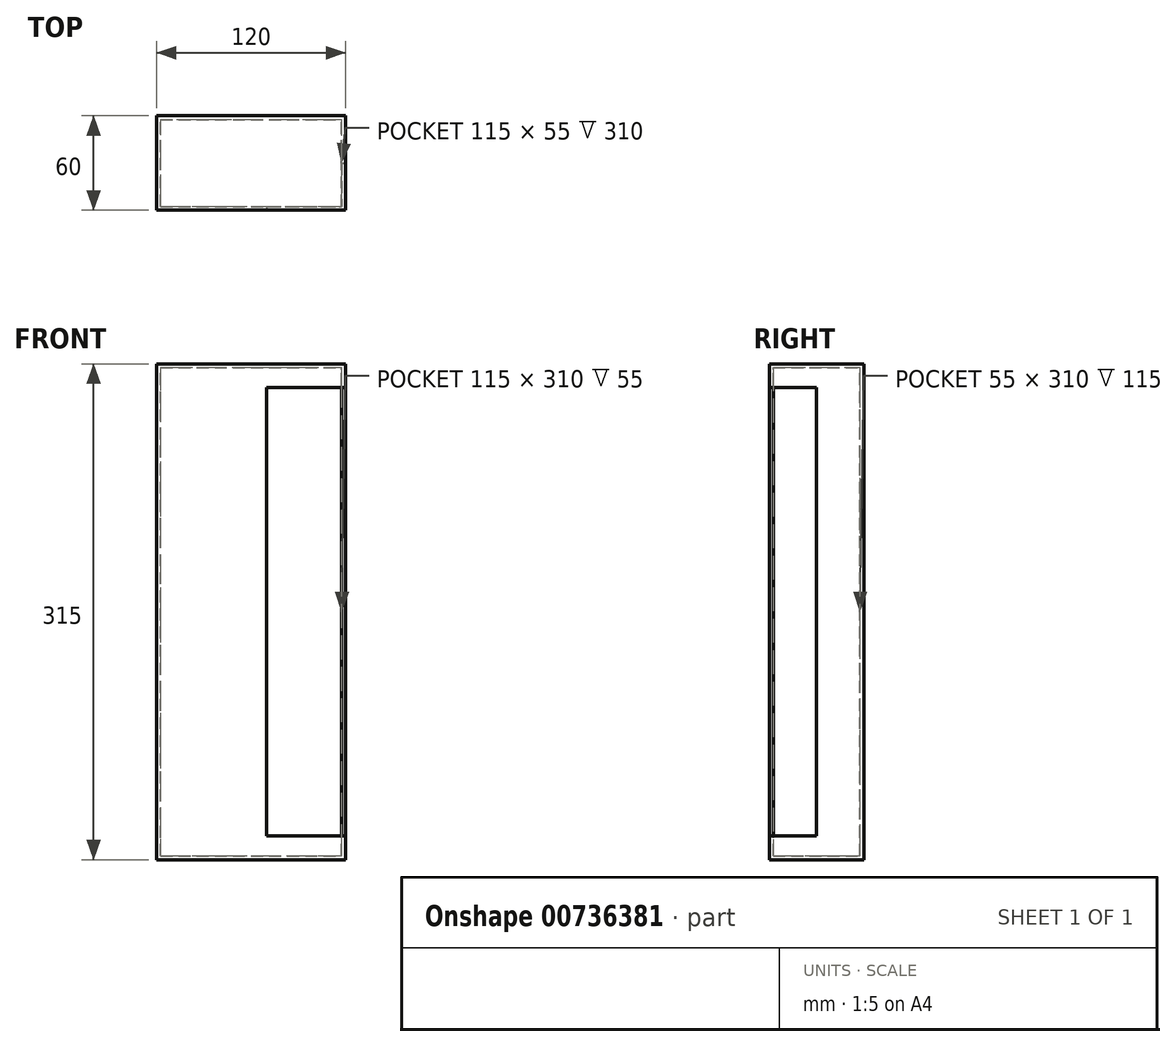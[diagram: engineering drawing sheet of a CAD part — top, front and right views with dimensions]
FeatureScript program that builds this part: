
annotation { "Feature Type Name" : "Feature", "Feature Type Description" : "" }
export const myFeature = defineFeature(function(context is Context, id is Id, definition is map)
    precondition{}
    {
        {
            var Q0;
            Q0=qCreatedBy(makeId("Front.planeOp"),FACE);
            var sketch = newSketch(context, id + "F0", { "sketchPlane" : qUnion([Q0])});
            skLineSegment(sketch, "E0.bottom", {"start": v(0, 0) * mm, "end": v(120, 0) * mm});
            skLineSegment(sketch, "E0.top", {"start": v(0, 315) * mm, "end": v(120, 315) * mm});
            skLineSegment(sketch, "E0.left", {"start": v(0, 0) * mm, "end": v(0, 315) * mm});
            skLineSegment(sketch, "E0.right", {"start": v(120, 0) * mm, "end": v(120, 315) * mm});
            skSolve(sketch);
        }
        {
            var Q0;
            Q0=makeQuery(id+"F0.imprint","IMPRINT",FACE,{"disambiguationData":[TD([[makeQuery(id+"F0.imprint","IMPRINT",EDGE,{"derivedFrom":sQuery(id+"F0.wireOp",EDGE,"E0.bottom")}),1.0]])]});
            extrude(context, id + "F1", {"entities" : qUnion([Q0]), "depth" : 60 * mm, "offsetDistance" : 25 * mm});
        }
        {
            var Q0;
            Q0=makeQuery(id+"F1.opExtrude","CAP_FACE",FACE,{"disambiguationData":[OSD([sQuery(id+"F0.wireOp",EDGE,"E0.bottom"),sQuery(id+"F0.wireOp",EDGE,"E0.top"),sQuery(id+"F0.wireOp",EDGE,"E0.left"),sQuery(id+"F0.wireOp",EDGE,"E0.right")])],"isStart":false});
            var sketch = newSketch(context, id + "F2", { "sketchPlane" : qUnion([Q0])});
            skLineSegment(sketch, "E1.bottom", {"start": v(70, 300) * mm, "end": v(170, 300) * mm});
            skLineSegment(sketch, "E1.top", {"start": v(70, 15) * mm, "end": v(170, 15) * mm});
            skLineSegment(sketch, "E1.left", {"start": v(70, 300) * mm, "end": v(70, 15) * mm});
            skLineSegment(sketch, "E1.right", {"start": v(170, 300) * mm, "end": v(170, 15) * mm});
            skPoint(sketch, "E1.middle", {"position": v(120, 157.5) * mm});
            skSolve(sketch);
        }
        {
            var Q0;
            Q0 = qSketchRegion(id + "F2", true);
            extrude(context, id + "F3", {"entities" : qUnion([Q0]), "operationType" : NewBodyOperationType.REMOVE, "oppositeDirection" : true, "depth" : 30 * mm, "offsetDistance" : 25 * mm});
        }
        {
            var Q0;
            Q0=makeQuery(id+"F3.boolean.opBoolean","COPY",FACE,{"derivedFrom":makeQuery(id+"F3.opExtrude","SWEPT_FACE",FACE,{"disambiguationData":[OSD([sQuery(id+"F2.wireOp",EDGE,"E1.bottom")])]})});
            var Q1;
            Q1=makeQuery(id+"F3.boolean.opBoolean","COPY",FACE,{"derivedFrom":makeQuery(id+"F3.opExtrude","SWEPT_FACE",FACE,{"disambiguationData":[OSD([sQuery(id+"F2.wireOp",EDGE,"E1.left")])]})});
            var Q2;
            Q2=makeQuery(id+"F3.boolean.opBoolean","COPY",FACE,{"derivedFrom":makeQuery(id+"F3.opExtrude","CAP_FACE",FACE,{"disambiguationData":[OSD([sQuery(id+"F2.wireOp",EDGE,"E1.bottom"),sQuery(id+"F2.wireOp",EDGE,"E1.top"),sQuery(id+"F2.wireOp",EDGE,"E1.left"),sQuery(id+"F2.wireOp",EDGE,"E1.right")])],"isStart":false})});
            var Q3;
            Q3=makeQuery(id+"F3.boolean.opBoolean","COPY",FACE,{"derivedFrom":makeQuery(id+"F3.opExtrude","SWEPT_FACE",FACE,{"disambiguationData":[OSD([sQuery(id+"F2.wireOp",EDGE,"E1.top")])]})});
            shell(context, id + "F4", {"entities" : qUnion([Q0, Q1, Q2, Q3]), "thickness" : 2.5 * mm});
        }
    });
